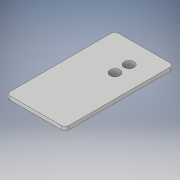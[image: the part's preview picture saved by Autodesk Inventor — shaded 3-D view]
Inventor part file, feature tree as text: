
AUTODESK INVENTOR PART (.ipt)
format: ipt  version: 2017.3 (Build 213257000, 257)  size: 153,600 bytes
history: native  units: mm
features: extrude x5, sketch x5, fillet x2
ambient origin geometry x8: Origin, YZ Plane, XZ Plane, XY Plane, X Axis, Y Axis, Z Axis, Center Point
bodies: Volumenkörper1 (feature_tree)
feature tree (12):
  extrude  "Extrusion1"  Depth=59.0mm
  extrude  "Extrusion2"  Depth=2.1mm
  extrude  "Extrusion3"  Depth=2.0mm TaperAngle=0.0deg
  fillet  "Rundung1"  Radius=5.4mm
  fillet  "Rundung2"  Radius=39.4mm
  extrude  "Extrusion4"  Depth=5.4mm
  extrude  "Extrusion5"  TaperAngle=0.0deg  [1 undecoded]
  sketch  "Skizze1"  dims[d0=32.0mm d1=59.0mm]
  sketch  "Skizze2"  dims[d2=2.0mm d3=0.0mm d4=2.1mm]
  sketch  "Skizze3"  dims[d5=2.1mm d6=2.0mm d7=0.0mm d8=5.4mm d9=39.4mm]
  sketch  "Skizze4"  dims[d11=10.2mm d12=5.4mm]
  sketch  "Skizze6"  dims[d13=7.62mm d14=0.0mm d15=0.0mm d16=1.0mm d17=2.0mm d18=20.0mm d19=3.5mm d20=29.8mm d21=6.01mm d22=0.0mm d29=2.0mm d30=2.5mm d31=4.01mm d32=6.01mm d33=0.0mm]
note: 1 required parameter value undecoded (feature->parameter linkage not recoverable at this tier; creation-order binding heuristic only, values carry confidence <= 0.55)
